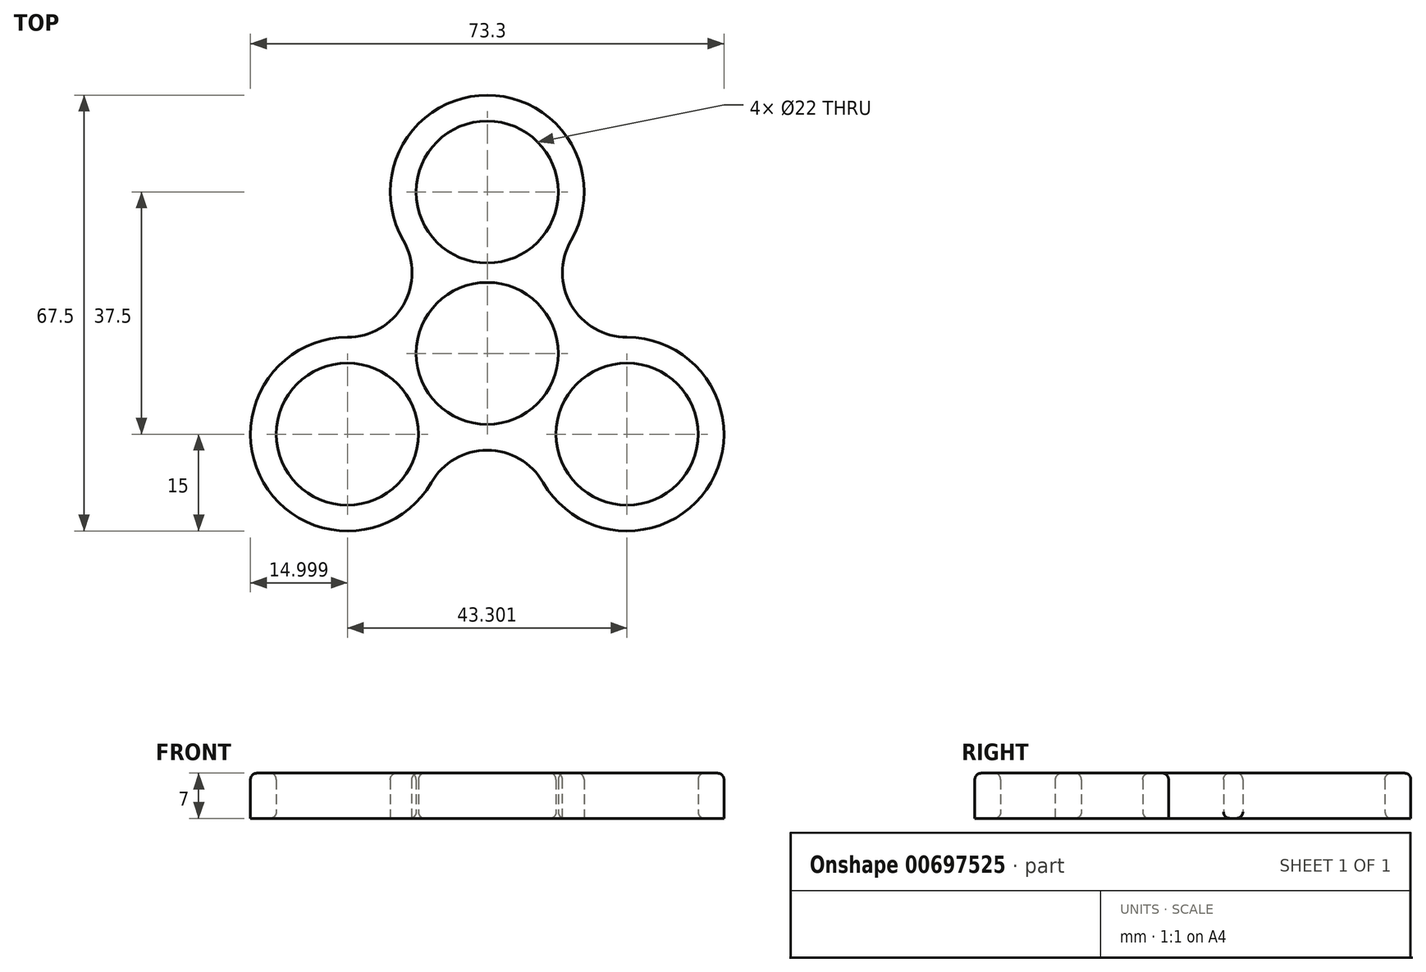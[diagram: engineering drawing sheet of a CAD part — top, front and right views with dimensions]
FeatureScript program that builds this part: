
annotation { "Feature Type Name" : "Feature", "Feature Type Description" : "" }
export const myFeature = defineFeature(function(context is Context, id is Id, definition is map)
    precondition{}
    {
        {
            var Q0;
            Q0=qCreatedBy(makeId("Top.planeOp"),FACE);
            var sketch = newSketch(context, id + "F0", { "sketchPlane" : qUnion([Q0])});
            skCircle(sketch, "E0", {"center": v(0, 0) * mm, "radius": 11 * mm});
            skArc(sketch, "E1", {"start": v(-8.3, 12.5) * mm, "mid": v(-13, 7.5) * mm, "end": v(-14.97, 0.93) * mm});
            skCircle(sketch, "E2", {"center": v(0, 25) * mm, "radius": 11 * mm});
            skArc(sketch, "E3", {"start": v(8.3, 12.5) * mm, "mid": v(0, 40) * mm, "end": v(-8.3, 12.5) * mm});
            skCircle(sketch, "E4", {"center": v(21.65, -12.5) * mm, "radius": 11 * mm});
            skArc(sketch, "E5", {"start": v(6.68, -13.43) * mm, "mid": v(34.64, -20) * mm, "end": v(14.97, 0.93) * mm});
            skCircle(sketch, "E6", {"center": v(-21.65, -12.5) * mm, "radius": 11 * mm});
            skArc(sketch, "E7", {"start": v(-14.97, 0.93) * mm, "mid": v(-34.64, -20) * mm, "end": v(-6.68, -13.43) * mm});
            skArc(sketch, "E8.trimOffspring", {"start": v(14.97, 0.93) * mm, "mid": v(13, 7.5) * mm, "end": v(8.3, 12.5) * mm});
            skArc(sketch, "E9.trimOffspring", {"start": v(-6.68, -13.43) * mm, "mid": v(0, -15) * mm, "end": v(6.68, -13.43) * mm});
            skSolve(sketch);
        }
        {
            var Q0;
            Q0 = qSketchRegion(id + "F0", true);
            extrude(context, id + "F1", {"entities" : qUnion([Q0]), "depth" : 7 * mm, "offsetDistance" : 25 * mm});
        }
        {
            var Q0;
            Q0=makeQuery(id+"F1.opExtrude","SWEPT_EDGE",EDGE,{"disambiguationData":[OSD([sQuery(id+"F0.wireOp",EDGE,"E1"),sQuery(id+"F0.wireOp",EDGE,"E7")])]});
            var Q1;
            Q1=makeQuery(id+"F1.opExtrude","SWEPT_EDGE",EDGE,{"disambiguationData":[OSD([sQuery(id+"F0.wireOp",EDGE,"E1"),sQuery(id+"F0.wireOp",EDGE,"E3")])]});
            var Q2;
            Q2=makeQuery(id+"F1.opExtrude","SWEPT_EDGE",EDGE,{"disambiguationData":[OSD([sQuery(id+"F0.wireOp",EDGE,"E3"),sQuery(id+"F0.wireOp",EDGE,"E8.trimOffspring")])]});
            var Q3;
            Q3=makeQuery(id+"F1.opExtrude","SWEPT_EDGE",EDGE,{"disambiguationData":[OSD([sQuery(id+"F0.wireOp",EDGE,"E5"),sQuery(id+"F0.wireOp",EDGE,"E8.trimOffspring")])]});
            var Q4;
            Q4=makeQuery(id+"F1.opExtrude","SWEPT_EDGE",EDGE,{"disambiguationData":[OSD([sQuery(id+"F0.wireOp",EDGE,"E5"),sQuery(id+"F0.wireOp",EDGE,"E9.trimOffspring")])]});
            var Q5;
            Q5=makeQuery(id+"F1.opExtrude","SWEPT_EDGE",EDGE,{"disambiguationData":[OSD([sQuery(id+"F0.wireOp",EDGE,"E7"),sQuery(id+"F0.wireOp",EDGE,"E9.trimOffspring")])]});
            fillet(context, id + "F2", {"entities" : qUnion([Q0, Q1, Q2, Q3, Q4, Q5]), "radius" : 10 * mm, "tangentPropagation" : true, "allowEdgeOverflow" : false});
        }
        {
            var Q0;
            Q0=makeQuery(id+"F1.opExtrude","CAP_EDGE",EDGE,{"disambiguationData":[OSD([sQuery(id+"F0.wireOp",EDGE,"E3")])],"isStart":false});
            var Q1;
            {var subQ0=sQuery(id+"F0.wireOp",EDGE,"E3");var subQ1=sQuery(id+"F0.wireOp",EDGE,"E1");Q1=makeQuery(id+"F2.opFillet","BLEND_EDGE",EDGE,{"blendedFrom":[makeQuery(id+"F1.opExtrude","SWEPT_EDGE",EDGE,{"disambiguationData":[OSD([subQ1,subQ0])]}),makeQuery(id+"F1.opExtrude","CAP_FACE",FACE,{"disambiguationData":[OSD([sQuery(id+"F0.wireOp",EDGE,"E0"),subQ1,sQuery(id+"F0.wireOp",EDGE,"E2"),subQ0,sQuery(id+"F0.wireOp",EDGE,"E4"),sQuery(id+"F0.wireOp",EDGE,"E5"),sQuery(id+"F0.wireOp",EDGE,"E6"),sQuery(id+"F0.wireOp",EDGE,"E7"),sQuery(id+"F0.wireOp",EDGE,"E8.trimOffspring"),sQuery(id+"F0.wireOp",EDGE,"E9.trimOffspring")])],"isStart":false})],"blendedInto":[makeQuery(id+"F1.opExtrude","CAP_FACE",FACE,{"disambiguationData":[OSD([sQuery(id+"F0.wireOp",EDGE,"E0"),subQ1,sQuery(id+"F0.wireOp",EDGE,"E2"),subQ0,sQuery(id+"F0.wireOp",EDGE,"E4"),sQuery(id+"F0.wireOp",EDGE,"E5"),sQuery(id+"F0.wireOp",EDGE,"E6"),sQuery(id+"F0.wireOp",EDGE,"E7"),sQuery(id+"F0.wireOp",EDGE,"E8.trimOffspring"),sQuery(id+"F0.wireOp",EDGE,"E9.trimOffspring")])],"isStart":false})]});}
            var Q2;
            {var subQ0=sQuery(id+"F0.wireOp",EDGE,"E8.trimOffspring");var subQ1=sQuery(id+"F0.wireOp",EDGE,"E5");Q2=makeQuery(id+"F2.opFillet","BLEND_EDGE",EDGE,{"blendedFrom":[makeQuery(id+"F1.opExtrude","SWEPT_EDGE",EDGE,{"disambiguationData":[OSD([subQ1,subQ0])]}),makeQuery(id+"F1.opExtrude","CAP_FACE",FACE,{"disambiguationData":[OSD([sQuery(id+"F0.wireOp",EDGE,"E0"),sQuery(id+"F0.wireOp",EDGE,"E1"),sQuery(id+"F0.wireOp",EDGE,"E2"),sQuery(id+"F0.wireOp",EDGE,"E3"),sQuery(id+"F0.wireOp",EDGE,"E4"),subQ1,sQuery(id+"F0.wireOp",EDGE,"E6"),sQuery(id+"F0.wireOp",EDGE,"E7"),subQ0,sQuery(id+"F0.wireOp",EDGE,"E9.trimOffspring")])],"isStart":true})],"blendedInto":[makeQuery(id+"F1.opExtrude","CAP_FACE",FACE,{"disambiguationData":[OSD([sQuery(id+"F0.wireOp",EDGE,"E0"),sQuery(id+"F0.wireOp",EDGE,"E1"),sQuery(id+"F0.wireOp",EDGE,"E2"),sQuery(id+"F0.wireOp",EDGE,"E3"),sQuery(id+"F0.wireOp",EDGE,"E4"),subQ1,sQuery(id+"F0.wireOp",EDGE,"E6"),sQuery(id+"F0.wireOp",EDGE,"E7"),subQ0,sQuery(id+"F0.wireOp",EDGE,"E9.trimOffspring")])],"isStart":true})]});}
            var Q3;
            Q3=makeQuery(id+"F1.opExtrude","CAP_EDGE",EDGE,{"disambiguationData":[OSD([sQuery(id+"F0.wireOp",EDGE,"E0")])],"isStart":true});
            var Q4;
            Q4=makeQuery(id+"F1.opExtrude","CAP_EDGE",EDGE,{"disambiguationData":[OSD([sQuery(id+"F0.wireOp",EDGE,"E0")])],"isStart":false});
            var Q5;
            Q5=makeQuery(id+"F1.opExtrude","CAP_EDGE",EDGE,{"disambiguationData":[OSD([sQuery(id+"F0.wireOp",EDGE,"E4")])],"isStart":false});
            var Q6;
            Q6=makeQuery(id+"F1.opExtrude","CAP_EDGE",EDGE,{"disambiguationData":[OSD([sQuery(id+"F0.wireOp",EDGE,"E4")])],"isStart":true});
            var Q7;
            Q7=makeQuery(id+"F1.opExtrude","CAP_EDGE",EDGE,{"disambiguationData":[OSD([sQuery(id+"F0.wireOp",EDGE,"E6")])],"isStart":true});
            var Q8;
            Q8=makeQuery(id+"F1.opExtrude","CAP_EDGE",EDGE,{"disambiguationData":[OSD([sQuery(id+"F0.wireOp",EDGE,"E6")])],"isStart":false});
            var Q9;
            Q9=makeQuery(id+"F1.opExtrude","CAP_EDGE",EDGE,{"disambiguationData":[OSD([sQuery(id+"F0.wireOp",EDGE,"E2")])],"isStart":true});
            var Q10;
            Q10=makeQuery(id+"F1.opExtrude","CAP_EDGE",EDGE,{"disambiguationData":[OSD([sQuery(id+"F0.wireOp",EDGE,"E2")])],"isStart":false});
            fillet(context, id + "F3", {"entities" : qUnion([Q0, Q1, Q2, Q3, Q4, Q5, Q6, Q7, Q8, Q9, Q10]), "radius" : 1 * mm, "tangentPropagation" : true, "allowEdgeOverflow" : false});
        }
    });
